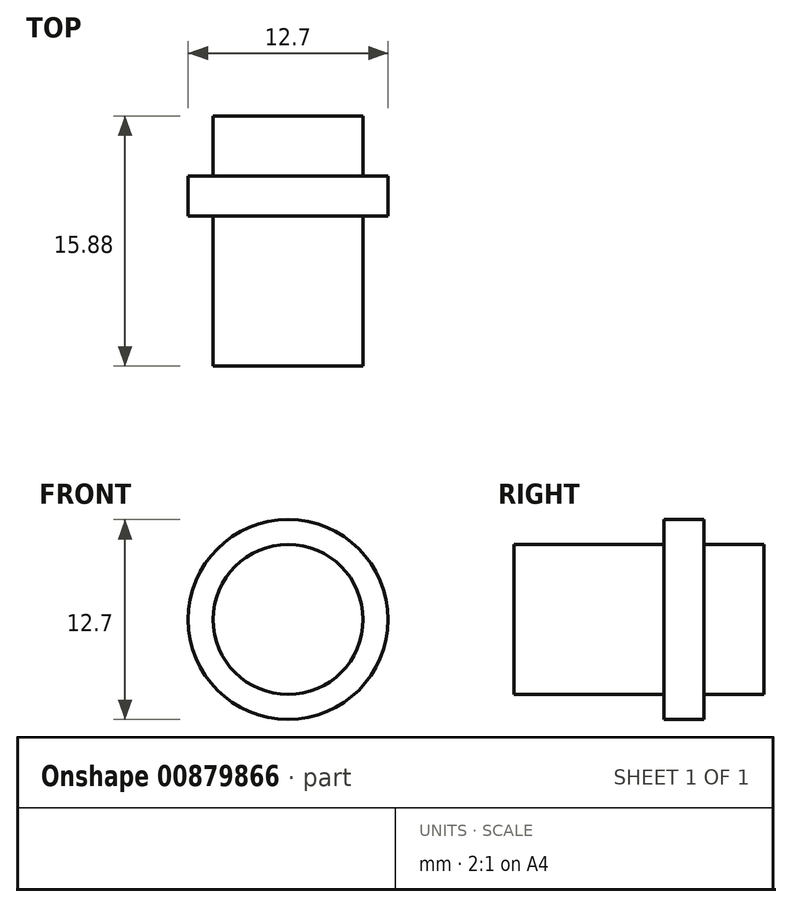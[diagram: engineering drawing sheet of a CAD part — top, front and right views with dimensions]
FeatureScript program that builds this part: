
annotation { "Feature Type Name" : "Feature", "Feature Type Description" : "" }
export const myFeature = defineFeature(function(context is Context, id is Id, definition is map)
    precondition{}
    {
        {
            var Q0;
            Q0=qCreatedBy(makeId("Front.planeOp"),FACE);
            var sketch = newSketch(context, id + "F0", { "sketchPlane" : qUnion([Q0])});
            skCircle(sketch, "E0", {"center": v(0, 0) * mm, "radius": 4.76 * mm});
            skSolve(sketch);
        }
        {
            var Q0;
            Q0 = qSketchRegion(id + "F0", true);
            extrude(context, id + "F1", {"entities" : qUnion([Q0]), "depth" : 9.52 * mm, "offsetDistance" : 25.4 * mm, "hasSecondDirection" : true, "secondDirectionOppositeDirection" : true, "secondDirectionDepth" : 6.35 * mm});
        }
        {
            var Q0;
            Q0=qCreatedBy(makeId("Front.planeOp"),FACE);
            var sketch = newSketch(context, id + "F2", { "sketchPlane" : qUnion([Q0])});
            skCircle(sketch, "E1", {"center": v(0, 0) * mm, "radius": 6.35 * mm});
            skSolve(sketch);
        }
        {
            var Q0;
            Q0 = qSketchRegion(id + "F2", true);
            extrude(context, id + "F3", {"entities" : qUnion([Q0]), "operationType" : NewBodyOperationType.ADD, "oppositeDirection" : true, "depth" : 2.54 * mm, "offsetDistance" : 25.4 * mm});
        }
    });
